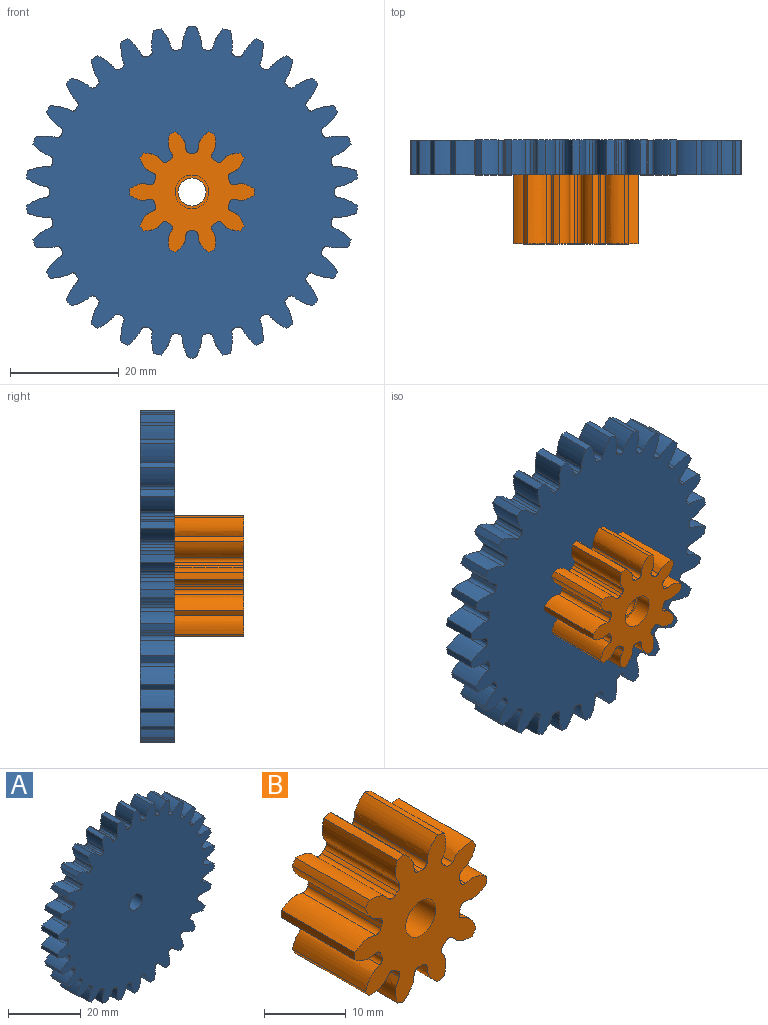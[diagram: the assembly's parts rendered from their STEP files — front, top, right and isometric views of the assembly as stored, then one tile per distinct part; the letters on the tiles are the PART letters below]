
ASSEMBLY  parts=2 mates=1
PART A: 185 faces, bbox 60.8x6.4x61 mm
  f0: cylinder r=2.59mm len=5.18mm, axis (0,-1,0), area 62.7mm2, adj f30,f183
  f1: cylinder r=30.48mm len=6.35mm, axis (0,1,0), area 8.9mm2, adj f30,f32,f173,f180
  f2: cylinder r=30.48mm len=6.35mm, axis (0,1,0), area 8.9mm2, adj f30,f32,f168,f175
  f3: cylinder r=30.48mm len=6.35mm, axis (0,1,0), area 8.9mm2, adj f30,f32,f163,f170
  f4: cylinder r=30.48mm len=6.35mm, axis (0,1,0), area 8.9mm2, adj f30,f32,f153,f165
  f5: cylinder r=30.48mm len=6.35mm, axis (0,1,0), area 8.9mm2, adj f30,f32,f148,f160
  f6: cylinder r=30.48mm len=6.35mm, axis (0,1,0), area 8.9mm2, adj f30,f32,f155,f158
  f7: cylinder r=30.48mm len=6.35mm, axis (0,1,0), area 8.9mm2, adj f30,f32,f143,f150
  f8: cylinder r=30.48mm len=6.35mm, axis (0,1,0), area 8.9mm2, adj f30,f32,f33,f145
  f9: cylinder r=30.48mm len=6.35mm, axis (0,1,0), area 8.9mm2, adj f30,f32,f128,f140
  f10: cylinder r=30.48mm len=6.35mm, axis (0,1,0), area 8.9mm2, adj f30,f32,f135,f138
  f11: cylinder r=30.48mm len=6.35mm, axis (0,1,0), area 8.9mm2, adj f30,f32,f123,f130
  f12: cylinder r=30.48mm len=6.35mm, axis (0,1,0), area 8.9mm2, adj f30,f32,f125,f178
  f13: cylinder r=30.48mm len=6.35mm, axis (0,1,0), area 8.9mm2, adj f30,f32,f120,f133
  f14: cylinder r=30.48mm len=6.35mm, axis (0,1,0), area 8.9mm2, adj f30,f32,f115,f118
  f15: cylinder r=30.48mm len=6.35mm, axis (0,1,0), area 8.9mm2, adj f30,f32,f110,f113
  f16: cylinder r=30.48mm len=6.35mm, axis (0,1,0), area 8.9mm2, adj f30,f32,f105,f108
  f17: cylinder r=30.48mm len=6.35mm, axis (0,1,0), area 8.9mm2, adj f30,f32,f88,f100
  f18: cylinder r=30.48mm len=6.35mm, axis (0,1,0), area 8.9mm2, adj f30,f32,f95,f98
  f19: cylinder r=30.48mm len=6.35mm, axis (0,1,0), area 8.9mm2, adj f30,f32,f83,f90
  f20: cylinder r=30.48mm len=6.35mm, axis (0,1,0), area 8.9mm2, adj f30,f32,f85,f103
  f21: cylinder r=30.48mm len=6.35mm, axis (0,1,0), area 8.9mm2, adj f30,f32,f80,f93
  f22: cylinder r=30.48mm len=6.35mm, axis (0,1,0), area 8.9mm2, adj f30,f32,f75,f78
  f23: cylinder r=30.48mm len=6.35mm, axis (0,1,0), area 8.9mm2, adj f30,f32,f70,f73
  f24: cylinder r=30.48mm len=6.35mm, axis (0,1,0), area 8.9mm2, adj f30,f32,f65,f68
  f25: cylinder r=30.48mm len=6.35mm, axis (0,1,0), area 8.9mm2, adj f30,f32,f53,f60
  f26: cylinder r=30.48mm len=6.35mm, axis (0,1,0), area 8.9mm2, adj f30,f32,f43,f55
  f27: cylinder r=30.48mm len=6.35mm, axis (0,1,0), area 8.9mm2, adj f30,f32,f50,f63
  f28: cylinder r=30.48mm len=6.35mm, axis (0,1,0), area 8.9mm2, adj f30,f32,f45,f48
  f29: cylinder r=30.48mm len=6.35mm, axis (0,1,0), area 8.9mm2, adj f30,f32,f40,f58
  f30: plane 60.96x60.76mm, normal (0,-1,0), area 2515.4mm2, adj f0,f1,f2,f3,f4,f5,f6,f7
  f31: cylinder r=30.48mm len=6.35mm, axis (0,1,0), area 8.9mm2, adj f30,f32,f35,f38
  f32: plane 60.96x60.76mm, normal (0,1,0), area 2506.3mm2, adj f1,f2,f3,f4,f5,f6,f7,f8
  f33: extruded ~6.35x3.53mm, area 24.5mm2, adj f8,f30,f32,f36
  f34: cylinder r=26.19mm len=6.35mm, axis (0,1,0), area 3.8mm2, adj f30,f32,f36,f37
  f35: extruded ~6.35x3.53mm, area 24.5mm2, adj f30,f31,f32,f37
  f36: cylinder r=0.7mm len=6.35mm, axis (0,1,0), area 6.8mm2, adj f30,f32,f33,f34
  f37: cylinder r=0.7mm len=6.35mm, axis (0,1,0), area 6.8mm2, adj f30,f32,f34,f35
  f38: extruded ~6.35x3.76mm, area 24.5mm2, adj f30,f31,f32,f41
  f39: cylinder r=26.19mm len=6.35mm, axis (0,1,0), area 3.8mm2, adj f30,f32,f41,f42
  f40: extruded ~6.35x3.15mm, area 24.5mm2, adj f29,f30,f32,f42
  f41: cylinder r=0.7mm len=6.35mm, axis (0,1,0), area 6.8mm2, adj f30,f32,f38,f39
  f42: cylinder r=0.7mm len=6.35mm, axis (0,1,0), area 6.8mm2, adj f30,f32,f39,f40
  f43: extruded ~6.35x3.46mm, area 24.5mm2, adj f26,f30,f32,f46
  f44: cylinder r=26.19mm len=6.35mm, axis (0,1,0), area 3.8mm2, adj f30,f32,f46,f47
  f45: extruded ~6.35x3.62mm, area 24.5mm2, adj f28,f30,f32,f47
  f46: cylinder r=0.7mm len=6.35mm, axis (0,1,0), area 6.8mm2, adj f30,f32,f43,f44
  f47: cylinder r=0.7mm len=6.35mm, axis (0,1,0), area 6.8mm2, adj f30,f32,f44,f45
  f48: extruded ~6.35x3.05mm, area 24.5mm2, adj f28,f30,f32,f51
  f49: cylinder r=26.19mm len=6.35mm, axis (0,1,0), area 3.8mm2, adj f30,f32,f51,f52
  f50: extruded ~6.35x3.8mm, area 24.5mm2, adj f27,f30,f32,f52
  f51: cylinder r=0.7mm len=6.35mm, axis (0,1,0), area 6.8mm2, adj f30,f32,f48,f49
  f52: cylinder r=0.7mm len=6.35mm, axis (0,1,0), area 6.8mm2, adj f30,f32,f49,f50
  f53: extruded ~6.35x3.73mm, area 24.5mm2, adj f25,f30,f32,f56
  f54: cylinder r=26.19mm len=6.35mm, axis (0,1,0), area 3.8mm2, adj f30,f32,f56,f57
  f55: extruded ~6.35x3.27mm, area 24.5mm2, adj f26,f30,f32,f57
  f56: cylinder r=0.7mm len=6.35mm, axis (0,1,0), area 6.8mm2, adj f30,f32,f53,f54
  f57: cylinder r=0.7mm len=6.35mm, axis (0,1,0), area 6.8mm2, adj f30,f32,f54,f55
  f58: extruded ~6.35x3.83mm, area 24.5mm2, adj f29,f30,f32,f61
  f59: cylinder r=26.19mm len=6.35mm, axis (0,1,0), area 3.8mm2, adj f30,f32,f61,f62
  f60: extruded ~6.35x2.79mm, area 24.5mm2, adj f25,f30,f32,f62
  f61: cylinder r=0.7mm len=6.35mm, axis (0,1,0), area 6.8mm2, adj f30,f32,f58,f59
  f62: cylinder r=0.7mm len=6.35mm, axis (0,1,0), area 6.8mm2, adj f30,f32,f59,f60
  f63: extruded ~6.35x2.9mm, area 24.5mm2, adj f27,f30,f32,f66
  f64: cylinder r=26.19mm len=6.35mm, axis (0,1,0), area 3.8mm2, adj f30,f32,f66,f67
  f65: extruded ~6.35x3.82mm, area 24.5mm2, adj f24,f30,f32,f67
  f66: cylinder r=0.7mm len=6.35mm, axis (0,1,0), area 6.8mm2, adj f30,f32,f63,f64
  f67: cylinder r=0.7mm len=6.35mm, axis (0,1,0), area 6.8mm2, adj f30,f32,f64,f65
  f68: extruded ~6.35x3.36mm, area 24.5mm2, adj f24,f30,f32,f71
  f69: cylinder r=26.19mm len=6.35mm, axis (0,1,0), area 3.8mm2, adj f30,f32,f71,f72
  f70: extruded ~6.35x3.67mm, area 24.5mm2, adj f23,f30,f32,f72
  f71: cylinder r=0.7mm len=6.35mm, axis (0,1,0), area 6.8mm2, adj f30,f32,f68,f69
  f72: cylinder r=0.7mm len=6.35mm, axis (0,1,0), area 6.8mm2, adj f30,f32,f69,f70
  f73: extruded ~6.35x3.67mm, area 24.5mm2, adj f23,f30,f32,f76
  f74: cylinder r=26.19mm len=6.35mm, axis (0,1,0), area 3.8mm2, adj f30,f32,f76,f77
  f75: extruded ~6.35x3.36mm, area 24.5mm2, adj f22,f30,f32,f77
  f76: cylinder r=0.7mm len=6.35mm, axis (0,1,0), area 6.8mm2, adj f30,f32,f73,f74
  f77: cylinder r=0.7mm len=6.35mm, axis (0,1,0), area 6.8mm2, adj f30,f32,f74,f75
  f78: extruded ~6.35x3.82mm, area 24.5mm2, adj f22,f30,f32,f81
  f79: cylinder r=26.19mm len=6.35mm, axis (0,1,0), area 3.8mm2, adj f30,f32,f81,f82
  f80: extruded ~6.35x2.9mm, area 24.5mm2, adj f21,f30,f32,f82
  f81: cylinder r=0.7mm len=6.35mm, axis (0,1,0), area 6.8mm2, adj f30,f32,f78,f79
  f82: cylinder r=0.7mm len=6.35mm, axis (0,1,0), area 6.8mm2, adj f30,f32,f79,f80
  f83: extruded ~6.35x2.79mm, area 24.5mm2, adj f19,f30,f32,f86
  f84: cylinder r=26.19mm len=6.35mm, axis (0,1,0), area 3.8mm2, adj f30,f32,f86,f87
  f85: extruded ~6.35x3.83mm, area 24.5mm2, adj f20,f30,f32,f87
  f86: cylinder r=0.7mm len=6.35mm, axis (0,1,0), area 6.8mm2, adj f30,f32,f83,f84
  f87: cylinder r=0.7mm len=6.35mm, axis (0,1,0), area 6.8mm2, adj f30,f32,f84,f85
  f88: extruded ~6.35x3.27mm, area 24.5mm2, adj f17,f30,f32,f91
  f89: cylinder r=26.19mm len=6.35mm, axis (0,1,0), area 3.8mm2, adj f30,f32,f91,f92
  f90: extruded ~6.35x3.73mm, area 24.5mm2, adj f19,f30,f32,f92
  f91: cylinder r=0.7mm len=6.35mm, axis (0,1,0), area 6.8mm2, adj f30,f32,f88,f89
  f92: cylinder r=0.7mm len=6.35mm, axis (0,1,0), area 6.8mm2, adj f30,f32,f89,f90
  f93: extruded ~6.35x3.8mm, area 24.5mm2, adj f21,f30,f32,f96
  f94: cylinder r=26.19mm len=6.35mm, axis (0,1,0), area 3.8mm2, adj f30,f32,f96,f97
  f95: extruded ~6.35x3.05mm, area 24.5mm2, adj f18,f30,f32,f97
  f96: cylinder r=0.7mm len=6.35mm, axis (0,1,0), area 6.8mm2, adj f30,f32,f93,f94
  f97: cylinder r=0.7mm len=6.35mm, axis (0,1,0), area 6.8mm2, adj f30,f32,f94,f95
  f98: extruded ~6.35x3.62mm, area 24.5mm2, adj f18,f30,f32,f101
  f99: cylinder r=26.19mm len=6.35mm, axis (0,1,0), area 3.8mm2, adj f30,f32,f101,f102
  f100: extruded ~6.35x3.46mm, area 24.5mm2, adj f17,f30,f32,f102
  f101: cylinder r=0.7mm len=6.35mm, axis (0,1,0), area 6.8mm2, adj f30,f32,f98,f99
  f102: cylinder r=0.7mm len=6.35mm, axis (0,1,0), area 6.8mm2, adj f30,f32,f99,f100
  f103: extruded ~6.35x3.15mm, area 24.5mm2, adj f20,f30,f32,f106
  f104: cylinder r=26.19mm len=6.35mm, axis (0,1,0), area 3.8mm2, adj f30,f32,f106,f107
  f105: extruded ~6.35x3.76mm, area 24.5mm2, adj f16,f30,f32,f107
  f106: cylinder r=0.7mm len=6.35mm, axis (0,1,0), area 6.8mm2, adj f30,f32,f103,f104
  f107: cylinder r=0.7mm len=6.35mm, axis (0,1,0), area 6.8mm2, adj f30,f32,f104,f105
  f108: extruded ~6.35x3.53mm, area 24.5mm2, adj f16,f30,f32,f111
  f109: cylinder r=26.19mm len=6.35mm, axis (0,1,0), area 3.8mm2, adj f30,f32,f111,f112
  f110: extruded ~6.35x3.53mm, area 24.5mm2, adj f15,f30,f32,f112
  f111: cylinder r=0.7mm len=6.35mm, axis (0,1,0), area 6.8mm2, adj f30,f32,f108,f109
  f112: cylinder r=0.7mm len=6.35mm, axis (0,1,0), area 6.8mm2, adj f30,f32,f109,f110
  f113: extruded ~6.35x3.76mm, area 24.5mm2, adj f15,f30,f32,f116
  f114: cylinder r=26.19mm len=6.35mm, axis (0,1,0), area 3.8mm2, adj f30,f32,f116,f117
  f115: extruded ~6.35x3.15mm, area 24.5mm2, adj f14,f30,f32,f117
  f116: cylinder r=0.7mm len=6.35mm, axis (0,1,0), area 6.8mm2, adj f30,f32,f113,f114
  f117: cylinder r=0.7mm len=6.35mm, axis (0,1,0), area 6.8mm2, adj f30,f32,f114,f115
  f118: extruded ~6.35x3.83mm, area 24.5mm2, adj f14,f30,f32,f121
  f119: cylinder r=26.19mm len=6.35mm, axis (0,1,0), area 3.8mm2, adj f30,f32,f121,f122
  f120: extruded ~6.35x2.79mm, area 24.5mm2, adj f13,f30,f32,f122
  f121: cylinder r=0.7mm len=6.35mm, axis (0,1,0), area 6.8mm2, adj f30,f32,f118,f119
  f122: cylinder r=0.7mm len=6.35mm, axis (0,1,0), area 6.8mm2, adj f30,f32,f119,f120
  f123: extruded ~6.35x2.9mm, area 24.5mm2, adj f11,f30,f32,f126
  f124: cylinder r=26.19mm len=6.35mm, axis (0,1,0), area 3.8mm2, adj f30,f32,f126,f127
  f125: extruded ~6.35x3.82mm, area 24.5mm2, adj f12,f30,f32,f127
  f126: cylinder r=0.7mm len=6.35mm, axis (0,1,0), area 6.8mm2, adj f30,f32,f123,f124
  f127: cylinder r=0.7mm len=6.35mm, axis (0,1,0), area 6.8mm2, adj f30,f32,f124,f125
  f128: extruded ~6.35x3.05mm, area 24.5mm2, adj f9,f30,f32,f131
  f129: cylinder r=26.19mm len=6.35mm, axis (0,1,0), area 3.8mm2, adj f30,f32,f131,f132
  f130: extruded ~6.35x3.8mm, area 24.5mm2, adj f11,f30,f32,f132
  f131: cylinder r=0.7mm len=6.35mm, axis (0,1,0), area 6.8mm2, adj f30,f32,f128,f129
  f132: cylinder r=0.7mm len=6.35mm, axis (0,1,0), area 6.8mm2, adj f30,f32,f129,f130
  f133: extruded ~6.35x3.73mm, area 24.5mm2, adj f13,f30,f32,f136
  f134: cylinder r=26.19mm len=6.35mm, axis (0,1,0), area 3.8mm2, adj f30,f32,f136,f137
  f135: extruded ~6.35x3.27mm, area 24.5mm2, adj f10,f30,f32,f137
  f136: cylinder r=0.7mm len=6.35mm, axis (0,1,0), area 6.8mm2, adj f30,f32,f133,f134
  f137: cylinder r=0.7mm len=6.35mm, axis (0,1,0), area 6.8mm2, adj f30,f32,f134,f135
  f138: extruded ~6.35x3.46mm, area 24.5mm2, adj f10,f30,f32,f141
  f139: cylinder r=26.19mm len=6.35mm, axis (0,1,0), area 3.8mm2, adj f30,f32,f141,f142
  f140: extruded ~6.35x3.62mm, area 24.5mm2, adj f9,f30,f32,f142
  f141: cylinder r=0.7mm len=6.35mm, axis (0,1,0), area 6.8mm2, adj f30,f32,f138,f139
  f142: cylinder r=0.7mm len=6.35mm, axis (0,1,0), area 6.8mm2, adj f30,f32,f139,f140
  f143: extruded ~6.35x3.15mm, area 24.5mm2, adj f7,f30,f32,f146
  f144: cylinder r=26.19mm len=6.35mm, axis (0,1,0), area 3.8mm2, adj f30,f32,f146,f147
  f145: extruded ~6.35x3.76mm, area 24.5mm2, adj f8,f30,f32,f147
  f146: cylinder r=0.7mm len=6.35mm, axis (0,1,0), area 6.8mm2, adj f30,f32,f143,f144
  f147: cylinder r=0.7mm len=6.35mm, axis (0,1,0), area 6.8mm2, adj f30,f32,f144,f145
  f148: extruded ~6.35x2.79mm, area 24.5mm2, adj f5,f30,f32,f151
  f149: cylinder r=26.19mm len=6.35mm, axis (0,1,0), area 3.8mm2, adj f30,f32,f151,f152
  f150: extruded ~6.35x3.83mm, area 24.5mm2, adj f7,f30,f32,f152
  f151: cylinder r=0.7mm len=6.35mm, axis (0,1,0), area 6.8mm2, adj f30,f32,f148,f149
  f152: cylinder r=0.7mm len=6.35mm, axis (0,1,0), area 6.8mm2, adj f30,f32,f149,f150
  f153: extruded ~6.35x3.62mm, area 24.5mm2, adj f4,f30,f32,f156
  f154: cylinder r=26.19mm len=6.35mm, axis (0,1,0), area 3.8mm2, adj f30,f32,f156,f157
  f155: extruded ~6.35x3.46mm, area 24.5mm2, adj f6,f30,f32,f157
  f156: cylinder r=0.7mm len=6.35mm, axis (0,1,0), area 6.8mm2, adj f30,f32,f153,f154
  f157: cylinder r=0.7mm len=6.35mm, axis (0,1,0), area 6.8mm2, adj f30,f32,f154,f155
  f158: extruded ~6.35x3.27mm, area 24.5mm2, adj f6,f30,f32,f161
  f159: cylinder r=26.19mm len=6.35mm, axis (0,1,0), area 3.8mm2, adj f30,f32,f161,f162
  f160: extruded ~6.35x3.73mm, area 24.5mm2, adj f5,f30,f32,f162
  f161: cylinder r=0.7mm len=6.35mm, axis (0,1,0), area 6.8mm2, adj f30,f32,f158,f159
  f162: cylinder r=0.7mm len=6.35mm, axis (0,1,0), area 6.8mm2, adj f30,f32,f159,f160
  f163: extruded ~6.35x3.8mm, area 24.5mm2, adj f3,f30,f32,f166
  f164: cylinder r=26.19mm len=6.35mm, axis (0,1,0), area 3.8mm2, adj f30,f32,f166,f167
  f165: extruded ~6.35x3.05mm, area 24.5mm2, adj f4,f30,f32,f167
  f166: cylinder r=0.7mm len=6.35mm, axis (0,1,0), area 6.8mm2, adj f30,f32,f163,f164
  f167: cylinder r=0.7mm len=6.35mm, axis (0,1,0), area 6.8mm2, adj f30,f32,f164,f165
  f168: extruded ~6.35x3.82mm, area 24.5mm2, adj f2,f30,f32,f171
  f169: cylinder r=26.19mm len=6.35mm, axis (0,1,0), area 3.8mm2, adj f30,f32,f171,f172
  f170: extruded ~6.35x2.9mm, area 24.5mm2, adj f3,f30,f32,f172
  f171: cylinder r=0.7mm len=6.35mm, axis (0,1,0), area 6.8mm2, adj f30,f32,f168,f169
  f172: cylinder r=0.7mm len=6.35mm, axis (0,1,0), area 6.8mm2, adj f30,f32,f169,f170
  f173: extruded ~6.35x3.67mm, area 24.5mm2, adj f1,f30,f32,f176
  f174: cylinder r=26.19mm len=6.35mm, axis (0,1,0), area 3.8mm2, adj f30,f32,f176,f177
  f175: extruded ~6.35x3.36mm, area 24.5mm2, adj f2,f30,f32,f177
  f176: cylinder r=0.7mm len=6.35mm, axis (0,1,0), area 6.8mm2, adj f30,f32,f173,f174
  f177: cylinder r=0.7mm len=6.35mm, axis (0,1,0), area 6.8mm2, adj f30,f32,f174,f175
  f178: extruded ~6.35x3.36mm, area 24.5mm2, adj f12,f30,f32,f181
  f179: cylinder r=26.19mm len=6.35mm, axis (0,1,0), area 3.8mm2, adj f30,f32,f181,f182
  f180: extruded ~6.35x3.67mm, area 24.5mm2, adj f1,f30,f32,f182
  f181: cylinder r=0.7mm len=6.35mm, axis (0,1,0), area 6.8mm2, adj f30,f32,f178,f179
  f182: cylinder r=0.7mm len=6.35mm, axis (0,1,0), area 6.8mm2, adj f30,f32,f179,f180
  f183: plane 6.2x6.2mm, normal (0,1,0), area 9.1mm2, adj f0,f184
  f184: cylinder r=3.1mm len=6.2mm, axis (0,1,0), area 48.7mm2, adj f32,f183
PART B: 65 faces, bbox 22.9x12.7x22.1 mm
  f0: cylinder r=2.58mm len=9.7mm, axis (0,-1,0), area 157.5mm2, adj f10,f63
  f1: cylinder r=11.43mm len=12.7mm, axis (0,1,0), area 14.2mm2, adj f10,f12,f15,f59
  f2: cylinder r=11.43mm len=12.7mm, axis (0,1,0), area 14.2mm2, adj f10,f12,f54,f60
  f3: cylinder r=11.43mm len=12.7mm, axis (0,1,0), area 14.2mm2, adj f10,f12,f45,f49
  f4: cylinder r=11.43mm len=12.7mm, axis (0,1,0), area 14.2mm2, adj f10,f12,f44,f55
  f5: cylinder r=11.43mm len=12.7mm, axis (0,1,0), area 14.2mm2, adj f10,f12,f35,f39
  f6: cylinder r=11.43mm len=12.7mm, axis (0,1,0), area 14.2mm2, adj f10,f12,f34,f50
  f7: cylinder r=11.43mm len=12.7mm, axis (0,1,0), area 14.2mm2, adj f10,f12,f29,f40
  f8: cylinder r=11.43mm len=12.7mm, axis (0,1,0), area 14.2mm2, adj f10,f12,f24,f30
  f9: cylinder r=11.43mm len=12.7mm, axis (0,1,0), area 14.2mm2, adj f10,f12,f19,f25
  f10: plane 22.9x22.11mm, normal (0,-1,0), area 251.7mm2, adj f0,f1,f2,f3,f4,f5,f6,f7
  f11: cylinder r=11.43mm len=12.7mm, axis (0,1,0), area 14.2mm2, adj f10,f12,f14,f20
  f12: plane 22.9x22.11mm, normal (0,1,0), area 242.4mm2, adj f1,f2,f3,f4,f5,f6,f7,f8
  f13: cylinder r=7.14mm len=12.7mm, axis (0,1,0), area 7.8mm2, adj f10,f12,f16,f17
  f14: extruded ~12.7x3.64mm, area 49.1mm2, adj f10,f11,f12,f16
  f15: extruded ~12.7x2.78mm, area 49.1mm2, adj f1,f10,f12,f17
  f16: cylinder r=0.78mm len=12.7mm, axis (0,1,0), area 14.7mm2, adj f10,f12,f13,f14
  f17: cylinder r=0.78mm len=12.7mm, axis (0,1,0), area 14.7mm2, adj f10,f12,f13,f15
  f18: cylinder r=7.14mm len=12.7mm, axis (0,1,0), area 7.8mm2, adj f10,f12,f21,f22
  f19: extruded ~12.7x2.78mm, area 49.1mm2, adj f9,f10,f12,f21
  f20: extruded ~12.7x3.64mm, area 49.1mm2, adj f10,f11,f12,f22
  f21: cylinder r=0.78mm len=12.7mm, axis (0,1,0), area 14.7mm2, adj f10,f12,f18,f19
  f22: cylinder r=0.78mm len=12.7mm, axis (0,1,0), area 14.7mm2, adj f10,f12,f18,f20
  f23: cylinder r=7.14mm len=12.7mm, axis (0,1,0), area 7.8mm2, adj f10,f12,f26,f27
  f24: extruded ~12.7x3.71mm, area 49.1mm2, adj f8,f10,f12,f26
  f25: extruded ~12.7x3.41mm, area 49.1mm2, adj f9,f10,f12,f27
  f26: cylinder r=0.78mm len=12.7mm, axis (0,1,0), area 14.7mm2, adj f10,f12,f23,f24
  f27: cylinder r=0.78mm len=12.7mm, axis (0,1,0), area 14.7mm2, adj f10,f12,f23,f25
  f28: cylinder r=7.14mm len=12.7mm, axis (0,1,0), area 7.8mm2, adj f10,f12,f31,f32
  f29: extruded ~12.7x3.22mm, area 49.1mm2, adj f7,f10,f12,f31
  f30: extruded ~12.7x3.22mm, area 49.1mm2, adj f8,f10,f12,f32
  f31: cylinder r=0.78mm len=12.7mm, axis (0,1,0), area 14.7mm2, adj f10,f12,f28,f29
  f32: cylinder r=0.78mm len=12.7mm, axis (0,1,0), area 14.7mm2, adj f10,f12,f28,f30
  f33: cylinder r=7.14mm len=12.7mm, axis (0,1,0), area 7.8mm2, adj f10,f12,f36,f37
  f34: extruded ~12.7x3.64mm, area 49.1mm2, adj f6,f10,f12,f36
  f35: extruded ~12.7x2.78mm, area 49.1mm2, adj f5,f10,f12,f37
  f36: cylinder r=0.78mm len=12.7mm, axis (0,1,0), area 14.7mm2, adj f10,f12,f33,f34
  f37: cylinder r=0.78mm len=12.7mm, axis (0,1,0), area 14.7mm2, adj f10,f12,f33,f35
  f38: cylinder r=7.14mm len=12.7mm, axis (0,1,0), area 7.8mm2, adj f10,f12,f41,f42
  f39: extruded ~12.7x3.41mm, area 49.1mm2, adj f5,f10,f12,f41
  f40: extruded ~12.7x3.71mm, area 49.1mm2, adj f7,f10,f12,f42
  f41: cylinder r=0.78mm len=12.7mm, axis (0,1,0), area 14.7mm2, adj f10,f12,f38,f39
  f42: cylinder r=0.78mm len=12.7mm, axis (0,1,0), area 14.7mm2, adj f10,f12,f38,f40
  f43: cylinder r=7.14mm len=12.7mm, axis (0,1,0), area 7.8mm2, adj f10,f12,f46,f47
  f44: extruded ~12.7x3.71mm, area 49.1mm2, adj f4,f10,f12,f46
  f45: extruded ~12.7x3.41mm, area 49.1mm2, adj f3,f10,f12,f47
  f46: cylinder r=0.78mm len=12.7mm, axis (0,1,0), area 14.7mm2, adj f10,f12,f43,f44
  f47: cylinder r=0.78mm len=12.7mm, axis (0,1,0), area 14.7mm2, adj f10,f12,f43,f45
  f48: cylinder r=7.14mm len=12.7mm, axis (0,1,0), area 7.8mm2, adj f10,f12,f51,f52
  f49: extruded ~12.7x2.78mm, area 49.1mm2, adj f3,f10,f12,f51
  f50: extruded ~12.7x3.64mm, area 49.1mm2, adj f6,f10,f12,f52
  f51: cylinder r=0.78mm len=12.7mm, axis (0,1,0), area 14.7mm2, adj f10,f12,f48,f49
  f52: cylinder r=0.78mm len=12.7mm, axis (0,1,0), area 14.7mm2, adj f10,f12,f48,f50
  f53: cylinder r=7.14mm len=12.7mm, axis (0,1,0), area 7.8mm2, adj f10,f12,f56,f57
  f54: extruded ~12.7x3.22mm, area 49.1mm2, adj f2,f10,f12,f56
  f55: extruded ~12.7x3.22mm, area 49.1mm2, adj f4,f10,f12,f57
  f56: cylinder r=0.78mm len=12.7mm, axis (0,1,0), area 14.7mm2, adj f10,f12,f53,f54
  f57: cylinder r=0.78mm len=12.7mm, axis (0,1,0), area 14.7mm2, adj f10,f12,f53,f55
  f58: cylinder r=7.14mm len=12.7mm, axis (0,1,0), area 7.8mm2, adj f10,f12,f61,f62
  f59: extruded ~12.7x3.41mm, area 49.1mm2, adj f1,f10,f12,f61
  f60: extruded ~12.7x3.71mm, area 49.1mm2, adj f2,f10,f12,f62
  f61: cylinder r=0.78mm len=12.7mm, axis (0,1,0), area 14.7mm2, adj f10,f12,f58,f59
  f62: cylinder r=0.78mm len=12.7mm, axis (0,1,0), area 14.7mm2, adj f10,f12,f58,f60
  f63: plane 6.2x6.2mm, normal (0,1,0), area 9.2mm2, adj f0,f64
  f64: cylinder r=3.1mm len=6.2mm, axis (0,1,0), area 58.4mm2, adj f12,f63
PLACE A at identity fixed
PLACE B rot(axis=(1,0,0),180deg) t=(0,-19.05,0)mm
MATE fastened A.f1 <-> B.f0  axis (0,-1,0) through (0,-6.35,0)mm
